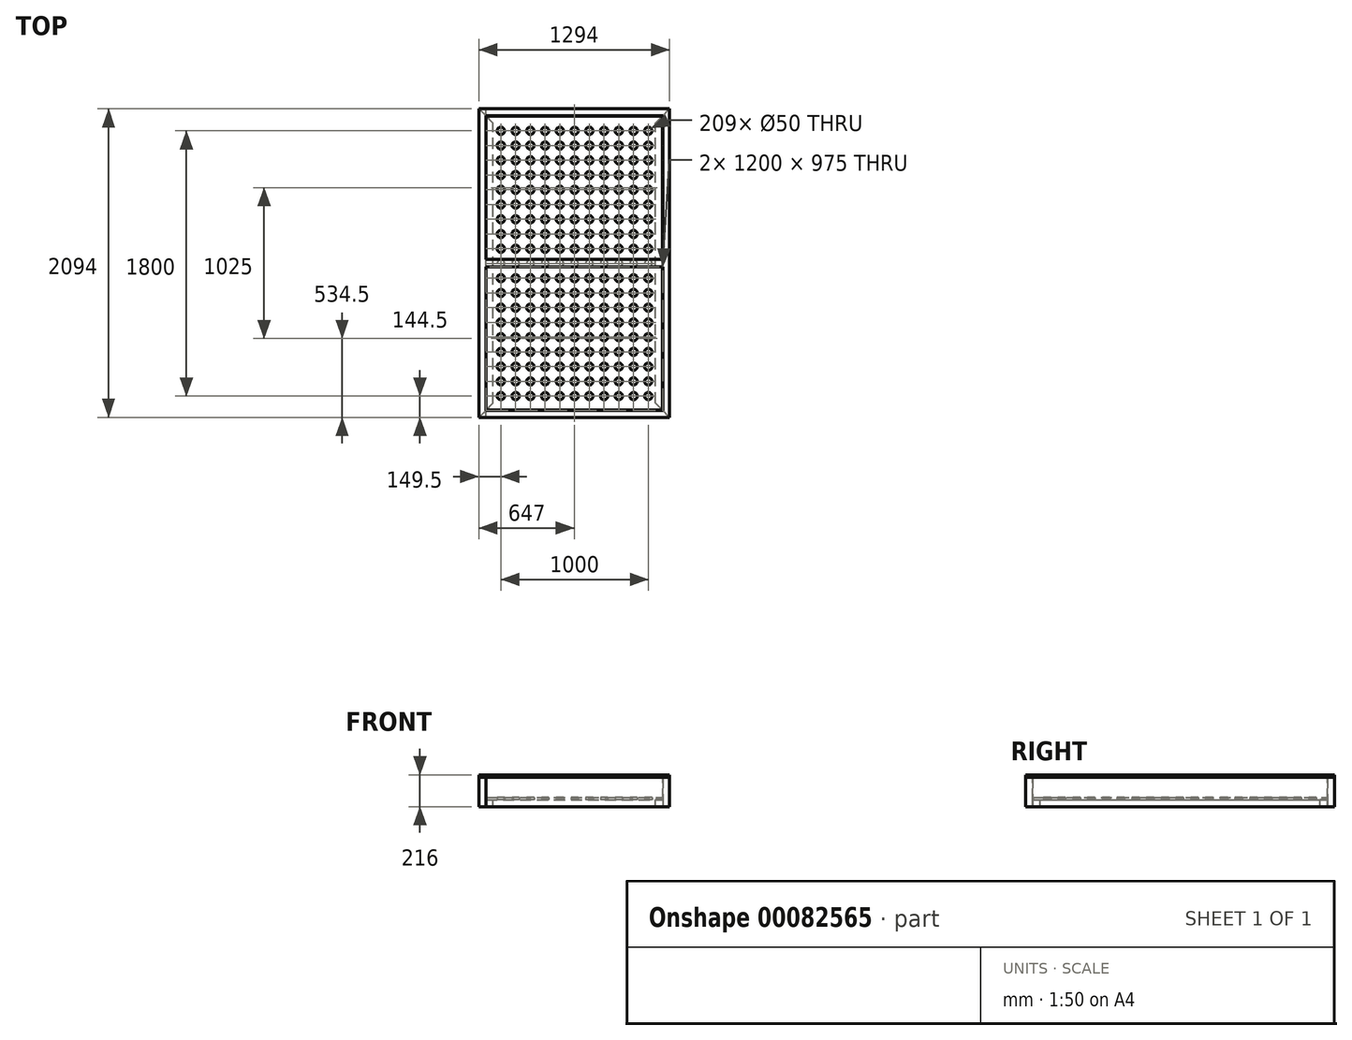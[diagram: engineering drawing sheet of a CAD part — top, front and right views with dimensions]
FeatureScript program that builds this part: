
annotation { "Feature Type Name" : "Feature", "Feature Type Description" : "" }
export const myFeature = defineFeature(function(context is Context, id is Id, definition is map)
    precondition{}
    {
        {
            var Q0;
            Q0=qCreatedBy(makeId("Front.planeOp"),FACE);
            var sketch = newSketch(context, id + "F0", { "sketchPlane" : qUnion([Q0])});
            skLineSegment(sketch, "E0.bottom", {"start": v(0, 0) * mm, "end": v(47, 0) * mm});
            skLineSegment(sketch, "E0.top", {"start": v(0, 200) * mm, "end": v(47, 200) * mm});
            skLineSegment(sketch, "E0.left", {"start": v(0, 0) * mm, "end": v(0, 200) * mm});
            skLineSegment(sketch, "E0.right", {"start": v(47, 0) * mm, "end": v(47, 200) * mm});
            skLineSegment(sketch, "E1", {"start": v(47, 0) * mm, "end": v(1247, 0) * mm, "construction": true});
            skLineSegment(sketch, "E2", {"start": v(647, 0) * mm, "end": v(647, 240.68) * mm, "construction": true});
            skLineSegment(sketch, "E3.bottom", {"start": v(47, 0) * mm, "end": v(97, 0) * mm});
            skLineSegment(sketch, "E3.top", {"start": v(47, 47) * mm, "end": v(97, 47) * mm});
            skLineSegment(sketch, "E3.left", {"start": v(47, 0) * mm, "end": v(47, 47) * mm});
            skLineSegment(sketch, "E3.right", {"start": v(97, 0) * mm, "end": v(97, 47) * mm});
            skLineSegment(sketch, "E4.MirrorCS", {"start": v(1294, 0) * mm, "end": v(1294, 200) * mm});
            skLineSegment(sketch, "E5.MirrorCS", {"start": v(1294, 0) * mm, "end": v(1247, 0) * mm});
            skLineSegment(sketch, "E6.MirrorCS", {"start": v(1247, 0) * mm, "end": v(1247, 200) * mm});
            skLineSegment(sketch, "E7.MirrorCS", {"start": v(1294, 200) * mm, "end": v(1247, 200) * mm});
            skLineSegment(sketch, "E8.MirrorCS", {"start": v(1247, 47) * mm, "end": v(1197, 47) * mm});
            skLineSegment(sketch, "E9.MirrorCS", {"start": v(1197, 0) * mm, "end": v(1197, 47) * mm});
            skLineSegment(sketch, "E10.MirrorCS", {"start": v(1247, 0) * mm, "end": v(1197, 0) * mm});
            skLineSegment(sketch, "E11.MirrorCS", {"start": v(1247, 0) * mm, "end": v(1247, 47) * mm});
            skSolve(sketch);
        }
        {
            var Q0;
            Q0 = qSketchRegion(id + "F0", true);
            extrude(context, id + "F1", {"entities" : qUnion([Q0]), "depth" : 2094 * mm});
        }
        {
            var Q0;
            Q0=makeQuery(id+"F1.opExtrude","SWEPT_FACE",FACE,{"disambiguationData":[OSD([sQuery(id+"F0.wireOp",EDGE,"E0.top")])]});
            var sketch = newSketch(context, id + "F2", { "sketchPlane" : qUnion([Q0])});
            skLineSegment(sketch, "E12", {"start": v(0, 0) * mm, "end": v(213.84, 0) * mm});
            skLineSegment(sketch, "E13", {"start": v(213.84, 0) * mm, "end": v(0, 0) * mm});
            skLineSegment(sketch, "E14", {"start": v(0, 0) * mm, "end": v(224.8, -224.8) * mm});
            skLineSegment(sketch, "E15", {"start": v(213.84, 0) * mm, "end": v(224.8, -224.8) * mm});
            skLineSegment(sketch, "E16", {"start": v(0, -2094) * mm, "end": v(120.3, -2094) * mm});
            skLineSegment(sketch, "E17", {"start": v(120.3, -2094) * mm, "end": v(0, -2094) * mm});
            skLineSegment(sketch, "E18", {"start": v(0, -2094) * mm, "end": v(152.65, -1941.35) * mm});
            skLineSegment(sketch, "E19", {"start": v(152.65, -1941.35) * mm, "end": v(120.3, -2094) * mm});
            skSolve(sketch);
        }
        {
            var Q0;
            {var subQ3=sQuery(id+"F2.wireOp",EDGE,"E15");Q0=makeQuery(id+"F2.imprint","IMPRINT",FACE,{"disambiguationData":[TD([[makeQuery(id+"F2.imprint","IMPRINT",EDGE,{"derivedFrom":subQ3}),-1.0]])]});}
            var Q1;
            {var subQ0=sQuery(id+"F2.wireOp",EDGE,"E14");var subQ1=sQuery(id+"F2.wireOp",EDGE,"E13");var subQ2=sQuery(id+"F0.wireOp",EDGE,"E0.top");var subQ3=makeQuery(id+"F2.imprint","INTERSECT",VERTEX,{"derivedFrom":[makeQuery(id+"F1.opExtrude","SWEPT_EDGE",EDGE,{"disambiguationData":[OSD([subQ2,sQuery(id+"F0.wireOp",EDGE,"E0.left")])]}),subQ1,subQ0]});Q1=makeQuery(id+"F2.imprint","IMPRINT",FACE,{"disambiguationData":[TD([[makeQuery(id+"F2.imprint","IMPRINT",EDGE,{"disambiguationData":[TD([[subQ3,-1.0]])],"derivedFrom":subQ1}),-1.0]])]});}
            var Q2;
            {var subQ0=sQuery(id+"F2.wireOp",EDGE,"E18");var subQ1=sQuery(id+"F2.wireOp",EDGE,"E17");var subQ2=sQuery(id+"F0.wireOp",EDGE,"E0.top");var subQ3=makeQuery(id+"F2.imprint","INTERSECT",VERTEX,{"derivedFrom":[makeQuery(id+"F1.opExtrude","SWEPT_EDGE",EDGE,{"disambiguationData":[OSD([subQ2,sQuery(id+"F0.wireOp",EDGE,"E0.left")])]}),subQ1,subQ0]});Q2=makeQuery(id+"F2.imprint","IMPRINT",FACE,{"disambiguationData":[TD([[makeQuery(id+"F2.imprint","IMPRINT",EDGE,{"disambiguationData":[TD([[subQ3,-1.0]])],"derivedFrom":subQ1}),1.0]])]});}
            var Q3;
            {var subQ3=sQuery(id+"F2.wireOp",EDGE,"E19");Q3=makeQuery(id+"F2.imprint","IMPRINT",FACE,{"disambiguationData":[TD([[makeQuery(id+"F2.imprint","IMPRINT",EDGE,{"derivedFrom":subQ3}),-1.0]])]});}
            extrude(context, id + "F3", {"entities" : qUnion([Q0, Q1, Q2, Q3]), "operationType" : NewBodyOperationType.REMOVE, "endBound" : BoundingType.THROUGH_ALL, "oppositeDirection" : true, "depth" : 25 * mm});
        }
        {
            var Q0;
            Q0=makeQuery(id+"F1.opExtrude","SWEPT_FACE",FACE,{"disambiguationData":[OSD([sQuery(id+"F0.wireOp",EDGE,"E7.MirrorCS")])]});
            var sketch = newSketch(context, id + "F4", { "sketchPlane" : qUnion([Q0])});
            skLineSegment(sketch, "E20", {"start": v(1294, 0) * mm, "end": v(937.7, 0) * mm});
            skLineSegment(sketch, "E21", {"start": v(937.7, 0) * mm, "end": v(937.7, -356.3) * mm});
            skLineSegment(sketch, "E22", {"start": v(937.7, -356.3) * mm, "end": v(1294, 0) * mm});
            skLineSegment(sketch, "E23", {"start": v(1294, -2094) * mm, "end": v(876.84, -2094) * mm});
            skLineSegment(sketch, "E24", {"start": v(876.84, -2094) * mm, "end": v(876.84, -1676.84) * mm});
            skLineSegment(sketch, "E25", {"start": v(876.84, -1676.84) * mm, "end": v(1294, -2094) * mm});
            skSolve(sketch);
        }
        {
            var Q0;
            Q0 = qSketchRegion(id + "F4", true);
            extrude(context, id + "F5", {"entities" : qUnion([Q0]), "operationType" : NewBodyOperationType.REMOVE, "endBound" : BoundingType.THROUGH_ALL, "oppositeDirection" : true, "depth" : 25 * mm});
        }
        {
            var Q0;
            Q0=qCreatedBy(makeId("Top.planeOp"),FACE);
            var sketch = newSketch(context, id + "F6", { "sketchPlane" : qUnion([Q0])});
            skLineSegment(sketch, "E26", {"start": v(0, 0) * mm, "end": v(1294, 0) * mm});
            skLineSegment(sketch, "E27", {"start": v(1294, 0) * mm, "end": v(1247, -47) * mm});
            skLineSegment(sketch, "E28", {"start": v(1247, -47) * mm, "end": v(47, -47) * mm});
            skLineSegment(sketch, "E29", {"start": v(47, -47) * mm, "end": v(0, 0) * mm});
            skLineSegment(sketch, "E30", {"start": v(1247, -2047) * mm, "end": v(1294, -2094) * mm});
            skLineSegment(sketch, "E31", {"start": v(1294, -2094) * mm, "end": v(0, -2094) * mm});
            skLineSegment(sketch, "E32", {"start": v(0, -2094) * mm, "end": v(47, -2047) * mm});
            skLineSegment(sketch, "E33", {"start": v(47, -2047) * mm, "end": v(1247, -2047) * mm});
            skLineSegment(sketch, "E34.0", {"start": v(0, 0) * mm, "end": v(47, -47) * mm});
            skSolve(sketch);
        }
        {
            var Q0;
            Q0 = qSketchRegion(id + "F6", true);
            extrude(context, id + "F7", {"entities" : qUnion([Q0]), "depth" : 200 * mm});
        }
        {
            var Q0;
            Q0=makeQuery(id+"F1.opExtrude","SWEPT_FACE",FACE,{"disambiguationData":[OSD([sQuery(id+"F0.wireOp",EDGE,"E8.MirrorCS")])]});
            var sketch = newSketch(context, id + "F8", { "sketchPlane" : qUnion([Q0])});
            skLineSegment(sketch, "E35.0", {"start": v(47, -2047) * mm, "end": v(47, -47) * mm});
            skLineSegment(sketch, "E36.0", {"start": v(1247, -2047) * mm, "end": v(1247, -47) * mm});
            skLineSegment(sketch, "E37", {"start": v(1247, -47) * mm, "end": v(47, -47) * mm});
            skLineSegment(sketch, "E38", {"start": v(47, -2047) * mm, "end": v(1247, -2047) * mm});
            skLineSegment(sketch, "E39.0", {"start": v(49.5, -2044.5) * mm, "end": v(49.5, -49.5) * mm});
            skLineSegment(sketch, "E39.1", {"start": v(49.5, -2044.5) * mm, "end": v(1244.5, -2044.5) * mm});
            skLineSegment(sketch, "E39.2", {"start": v(1244.5, -2044.5) * mm, "end": v(1244.5, -49.5) * mm});
            skLineSegment(sketch, "E39.3", {"start": v(1244.5, -49.5) * mm, "end": v(49.5, -49.5) * mm});
            skCircle(sketch, "E40", {"center": v(149.5, -149.5) * mm, "radius": 25 * mm});
            skCircle(sketch, "E41.0.1.0", {"center": v(149.5, -249.5) * mm, "radius": 25 * mm});
            skCircle(sketch, "E41.0.2.0", {"center": v(149.5, -349.5) * mm, "radius": 25 * mm});
            skCircle(sketch, "E41.0.3.0", {"center": v(149.5, -449.5) * mm, "radius": 25 * mm});
            skCircle(sketch, "E41.0.4.0", {"center": v(149.5, -549.5) * mm, "radius": 25 * mm});
            skCircle(sketch, "E41.0.5.0", {"center": v(149.5, -649.5) * mm, "radius": 25 * mm});
            skCircle(sketch, "E41.0.6.0", {"center": v(149.5, -749.5) * mm, "radius": 25 * mm});
            skCircle(sketch, "E41.0.7.0", {"center": v(149.5, -849.5) * mm, "radius": 25 * mm});
            skCircle(sketch, "E41.0.8.0", {"center": v(149.5, -949.5) * mm, "radius": 25 * mm});
            skCircle(sketch, "E41.0.9.0", {"center": v(149.5, -1049.5) * mm, "radius": 25 * mm});
            skCircle(sketch, "E41.0.10.0", {"center": v(149.5, -1149.5) * mm, "radius": 25 * mm});
            skCircle(sketch, "E41.0.11.0", {"center": v(149.5, -1249.5) * mm, "radius": 25 * mm});
            skCircle(sketch, "E41.0.12.0", {"center": v(149.5, -1349.5) * mm, "radius": 25 * mm});
            skCircle(sketch, "E41.0.13.0", {"center": v(149.5, -1449.5) * mm, "radius": 25 * mm});
            skCircle(sketch, "E41.0.14.0", {"center": v(149.5, -1549.5) * mm, "radius": 25 * mm});
            skCircle(sketch, "E41.0.15.0", {"center": v(149.5, -1649.5) * mm, "radius": 25 * mm});
            skCircle(sketch, "E41.0.16.0", {"center": v(149.5, -1749.5) * mm, "radius": 25 * mm});
            skCircle(sketch, "E41.0.17.0", {"center": v(149.5, -1849.5) * mm, "radius": 25 * mm});
            skCircle(sketch, "E41.0.18.0", {"center": v(149.5, -1949.5) * mm, "radius": 25 * mm});
            skCircle(sketch, "E41.1.0.0", {"center": v(249.5, -149.5) * mm, "radius": 25 * mm});
            skCircle(sketch, "E41.1.1.0", {"center": v(249.5, -249.5) * mm, "radius": 25 * mm});
            skCircle(sketch, "E41.1.2.0", {"center": v(249.5, -349.5) * mm, "radius": 25 * mm});
            skCircle(sketch, "E41.1.3.0", {"center": v(249.5, -449.5) * mm, "radius": 25 * mm});
            skCircle(sketch, "E41.1.4.0", {"center": v(249.5, -549.5) * mm, "radius": 25 * mm});
            skCircle(sketch, "E41.1.5.0", {"center": v(249.5, -649.5) * mm, "radius": 25 * mm});
            skCircle(sketch, "E41.1.6.0", {"center": v(249.5, -749.5) * mm, "radius": 25 * mm});
            skCircle(sketch, "E41.1.7.0", {"center": v(249.5, -849.5) * mm, "radius": 25 * mm});
            skCircle(sketch, "E41.1.8.0", {"center": v(249.5, -949.5) * mm, "radius": 25 * mm});
            skCircle(sketch, "E41.1.9.0", {"center": v(249.5, -1049.5) * mm, "radius": 25 * mm});
            skCircle(sketch, "E41.1.10.0", {"center": v(249.5, -1149.5) * mm, "radius": 25 * mm});
            skCircle(sketch, "E41.1.11.0", {"center": v(249.5, -1249.5) * mm, "radius": 25 * mm});
            skCircle(sketch, "E41.1.12.0", {"center": v(249.5, -1349.5) * mm, "radius": 25 * mm});
            skCircle(sketch, "E41.1.13.0", {"center": v(249.5, -1449.5) * mm, "radius": 25 * mm});
            skCircle(sketch, "E41.1.14.0", {"center": v(249.5, -1549.5) * mm, "radius": 25 * mm});
            skCircle(sketch, "E41.1.15.0", {"center": v(249.5, -1649.5) * mm, "radius": 25 * mm});
            skCircle(sketch, "E41.1.16.0", {"center": v(249.5, -1749.5) * mm, "radius": 25 * mm});
            skCircle(sketch, "E41.1.17.0", {"center": v(249.5, -1849.5) * mm, "radius": 25 * mm});
            skCircle(sketch, "E41.1.18.0", {"center": v(249.5, -1949.5) * mm, "radius": 25 * mm});
            skCircle(sketch, "E41.2.0.0", {"center": v(349.5, -149.5) * mm, "radius": 25 * mm});
            skCircle(sketch, "E41.2.1.0", {"center": v(349.5, -249.5) * mm, "radius": 25 * mm});
            skCircle(sketch, "E41.2.2.0", {"center": v(349.5, -349.5) * mm, "radius": 25 * mm});
            skCircle(sketch, "E41.2.3.0", {"center": v(349.5, -449.5) * mm, "radius": 25 * mm});
            skCircle(sketch, "E41.2.4.0", {"center": v(349.5, -549.5) * mm, "radius": 25 * mm});
            skCircle(sketch, "E41.2.5.0", {"center": v(349.5, -649.5) * mm, "radius": 25 * mm});
            skCircle(sketch, "E41.2.6.0", {"center": v(349.5, -749.5) * mm, "radius": 25 * mm});
            skCircle(sketch, "E41.2.7.0", {"center": v(349.5, -849.5) * mm, "radius": 25 * mm});
            skCircle(sketch, "E41.2.8.0", {"center": v(349.5, -949.5) * mm, "radius": 25 * mm});
            skCircle(sketch, "E41.2.9.0", {"center": v(349.5, -1049.5) * mm, "radius": 25 * mm});
            skCircle(sketch, "E41.2.10.0", {"center": v(349.5, -1149.5) * mm, "radius": 25 * mm});
            skCircle(sketch, "E41.2.11.0", {"center": v(349.5, -1249.5) * mm, "radius": 25 * mm});
            skCircle(sketch, "E41.2.12.0", {"center": v(349.5, -1349.5) * mm, "radius": 25 * mm});
            skCircle(sketch, "E41.2.13.0", {"center": v(349.5, -1449.5) * mm, "radius": 25 * mm});
            skCircle(sketch, "E41.2.14.0", {"center": v(349.5, -1549.5) * mm, "radius": 25 * mm});
            skCircle(sketch, "E41.2.15.0", {"center": v(349.5, -1649.5) * mm, "radius": 25 * mm});
            skCircle(sketch, "E41.2.16.0", {"center": v(349.5, -1749.5) * mm, "radius": 25 * mm});
            skCircle(sketch, "E41.2.17.0", {"center": v(349.5, -1849.5) * mm, "radius": 25 * mm});
            skCircle(sketch, "E41.2.18.0", {"center": v(349.5, -1949.5) * mm, "radius": 25 * mm});
            skCircle(sketch, "E41.3.0.0", {"center": v(449.5, -149.5) * mm, "radius": 25 * mm});
            skCircle(sketch, "E41.3.1.0", {"center": v(449.5, -249.5) * mm, "radius": 25 * mm});
            skCircle(sketch, "E41.3.2.0", {"center": v(449.5, -349.5) * mm, "radius": 25 * mm});
            skCircle(sketch, "E41.3.3.0", {"center": v(449.5, -449.5) * mm, "radius": 25 * mm});
            skCircle(sketch, "E41.3.4.0", {"center": v(449.5, -549.5) * mm, "radius": 25 * mm});
            skCircle(sketch, "E41.3.5.0", {"center": v(449.5, -649.5) * mm, "radius": 25 * mm});
            skCircle(sketch, "E41.3.6.0", {"center": v(449.5, -749.5) * mm, "radius": 25 * mm});
            skCircle(sketch, "E41.3.7.0", {"center": v(449.5, -849.5) * mm, "radius": 25 * mm});
            skCircle(sketch, "E41.3.8.0", {"center": v(449.5, -949.5) * mm, "radius": 25 * mm});
            skCircle(sketch, "E41.3.9.0", {"center": v(449.5, -1049.5) * mm, "radius": 25 * mm});
            skCircle(sketch, "E41.3.10.0", {"center": v(449.5, -1149.5) * mm, "radius": 25 * mm});
            skCircle(sketch, "E41.3.11.0", {"center": v(449.5, -1249.5) * mm, "radius": 25 * mm});
            skCircle(sketch, "E41.3.12.0", {"center": v(449.5, -1349.5) * mm, "radius": 25 * mm});
            skCircle(sketch, "E41.3.13.0", {"center": v(449.5, -1449.5) * mm, "radius": 25 * mm});
            skCircle(sketch, "E41.3.14.0", {"center": v(449.5, -1549.5) * mm, "radius": 25 * mm});
            skCircle(sketch, "E41.3.15.0", {"center": v(449.5, -1649.5) * mm, "radius": 25 * mm});
            skCircle(sketch, "E41.3.16.0", {"center": v(449.5, -1749.5) * mm, "radius": 25 * mm});
            skCircle(sketch, "E41.3.17.0", {"center": v(449.5, -1849.5) * mm, "radius": 25 * mm});
            skCircle(sketch, "E41.3.18.0", {"center": v(449.5, -1949.5) * mm, "radius": 25 * mm});
            skCircle(sketch, "E41.4.0.0", {"center": v(549.5, -149.5) * mm, "radius": 25 * mm});
            skCircle(sketch, "E41.4.1.0", {"center": v(549.5, -249.5) * mm, "radius": 25 * mm});
            skCircle(sketch, "E41.4.2.0", {"center": v(549.5, -349.5) * mm, "radius": 25 * mm});
            skCircle(sketch, "E41.4.3.0", {"center": v(549.5, -449.5) * mm, "radius": 25 * mm});
            skCircle(sketch, "E41.4.4.0", {"center": v(549.5, -549.5) * mm, "radius": 25 * mm});
            skCircle(sketch, "E41.4.5.0", {"center": v(549.5, -649.5) * mm, "radius": 25 * mm});
            skCircle(sketch, "E41.4.6.0", {"center": v(549.5, -749.5) * mm, "radius": 25 * mm});
            skCircle(sketch, "E41.4.7.0", {"center": v(549.5, -849.5) * mm, "radius": 25 * mm});
            skCircle(sketch, "E41.4.8.0", {"center": v(549.5, -949.5) * mm, "radius": 25 * mm});
            skCircle(sketch, "E41.4.9.0", {"center": v(549.5, -1049.5) * mm, "radius": 25 * mm});
            skCircle(sketch, "E41.4.10.0", {"center": v(549.5, -1149.5) * mm, "radius": 25 * mm});
            skCircle(sketch, "E41.4.11.0", {"center": v(549.5, -1249.5) * mm, "radius": 25 * mm});
            skCircle(sketch, "E41.4.12.0", {"center": v(549.5, -1349.5) * mm, "radius": 25 * mm});
            skCircle(sketch, "E41.4.13.0", {"center": v(549.5, -1449.5) * mm, "radius": 25 * mm});
            skCircle(sketch, "E41.4.14.0", {"center": v(549.5, -1549.5) * mm, "radius": 25 * mm});
            skCircle(sketch, "E41.4.15.0", {"center": v(549.5, -1649.5) * mm, "radius": 25 * mm});
            skCircle(sketch, "E41.4.16.0", {"center": v(549.5, -1749.5) * mm, "radius": 25 * mm});
            skCircle(sketch, "E41.4.17.0", {"center": v(549.5, -1849.5) * mm, "radius": 25 * mm});
            skCircle(sketch, "E41.4.18.0", {"center": v(549.5, -1949.5) * mm, "radius": 25 * mm});
            skCircle(sketch, "E41.5.0.0", {"center": v(649.5, -149.5) * mm, "radius": 25 * mm});
            skCircle(sketch, "E41.5.1.0", {"center": v(649.5, -249.5) * mm, "radius": 25 * mm});
            skCircle(sketch, "E41.5.2.0", {"center": v(649.5, -349.5) * mm, "radius": 25 * mm});
            skCircle(sketch, "E41.5.3.0", {"center": v(649.5, -449.5) * mm, "radius": 25 * mm});
            skCircle(sketch, "E41.5.4.0", {"center": v(649.5, -549.5) * mm, "radius": 25 * mm});
            skCircle(sketch, "E41.5.5.0", {"center": v(649.5, -649.5) * mm, "radius": 25 * mm});
            skCircle(sketch, "E41.5.6.0", {"center": v(649.5, -749.5) * mm, "radius": 25 * mm});
            skCircle(sketch, "E41.5.7.0", {"center": v(649.5, -849.5) * mm, "radius": 25 * mm});
            skCircle(sketch, "E41.5.8.0", {"center": v(649.5, -949.5) * mm, "radius": 25 * mm});
            skCircle(sketch, "E41.5.9.0", {"center": v(649.5, -1049.5) * mm, "radius": 25 * mm});
            skCircle(sketch, "E41.5.10.0", {"center": v(649.5, -1149.5) * mm, "radius": 25 * mm});
            skCircle(sketch, "E41.5.11.0", {"center": v(649.5, -1249.5) * mm, "radius": 25 * mm});
            skCircle(sketch, "E41.5.12.0", {"center": v(649.5, -1349.5) * mm, "radius": 25 * mm});
            skCircle(sketch, "E41.5.13.0", {"center": v(649.5, -1449.5) * mm, "radius": 25 * mm});
            skCircle(sketch, "E41.5.14.0", {"center": v(649.5, -1549.5) * mm, "radius": 25 * mm});
            skCircle(sketch, "E41.5.15.0", {"center": v(649.5, -1649.5) * mm, "radius": 25 * mm});
            skCircle(sketch, "E41.5.16.0", {"center": v(649.5, -1749.5) * mm, "radius": 25 * mm});
            skCircle(sketch, "E41.5.17.0", {"center": v(649.5, -1849.5) * mm, "radius": 25 * mm});
            skCircle(sketch, "E41.5.18.0", {"center": v(649.5, -1949.5) * mm, "radius": 25 * mm});
            skCircle(sketch, "E41.6.0.0", {"center": v(749.5, -149.5) * mm, "radius": 25 * mm});
            skCircle(sketch, "E41.6.1.0", {"center": v(749.5, -249.5) * mm, "radius": 25 * mm});
            skCircle(sketch, "E41.6.2.0", {"center": v(749.5, -349.5) * mm, "radius": 25 * mm});
            skCircle(sketch, "E41.6.3.0", {"center": v(749.5, -449.5) * mm, "radius": 25 * mm});
            skCircle(sketch, "E41.6.4.0", {"center": v(749.5, -549.5) * mm, "radius": 25 * mm});
            skCircle(sketch, "E41.6.5.0", {"center": v(749.5, -649.5) * mm, "radius": 25 * mm});
            skCircle(sketch, "E41.6.6.0", {"center": v(749.5, -749.5) * mm, "radius": 25 * mm});
            skCircle(sketch, "E41.6.7.0", {"center": v(749.5, -849.5) * mm, "radius": 25 * mm});
            skCircle(sketch, "E41.6.8.0", {"center": v(749.5, -949.5) * mm, "radius": 25 * mm});
            skCircle(sketch, "E41.6.9.0", {"center": v(749.5, -1049.5) * mm, "radius": 25 * mm});
            skCircle(sketch, "E41.6.10.0", {"center": v(749.5, -1149.5) * mm, "radius": 25 * mm});
            skCircle(sketch, "E41.6.11.0", {"center": v(749.5, -1249.5) * mm, "radius": 25 * mm});
            skCircle(sketch, "E41.6.12.0", {"center": v(749.5, -1349.5) * mm, "radius": 25 * mm});
            skCircle(sketch, "E41.6.13.0", {"center": v(749.5, -1449.5) * mm, "radius": 25 * mm});
            skCircle(sketch, "E41.6.14.0", {"center": v(749.5, -1549.5) * mm, "radius": 25 * mm});
            skCircle(sketch, "E41.6.15.0", {"center": v(749.5, -1649.5) * mm, "radius": 25 * mm});
            skCircle(sketch, "E41.6.16.0", {"center": v(749.5, -1749.5) * mm, "radius": 25 * mm});
            skCircle(sketch, "E41.6.17.0", {"center": v(749.5, -1849.5) * mm, "radius": 25 * mm});
            skCircle(sketch, "E41.6.18.0", {"center": v(749.5, -1949.5) * mm, "radius": 25 * mm});
            skCircle(sketch, "E41.7.0.0", {"center": v(849.5, -149.5) * mm, "radius": 25 * mm});
            skCircle(sketch, "E41.7.1.0", {"center": v(849.5, -249.5) * mm, "radius": 25 * mm});
            skCircle(sketch, "E41.7.2.0", {"center": v(849.5, -349.5) * mm, "radius": 25 * mm});
            skCircle(sketch, "E41.7.3.0", {"center": v(849.5, -449.5) * mm, "radius": 25 * mm});
            skCircle(sketch, "E41.7.4.0", {"center": v(849.5, -549.5) * mm, "radius": 25 * mm});
            skCircle(sketch, "E41.7.5.0", {"center": v(849.5, -649.5) * mm, "radius": 25 * mm});
            skCircle(sketch, "E41.7.6.0", {"center": v(849.5, -749.5) * mm, "radius": 25 * mm});
            skCircle(sketch, "E41.7.7.0", {"center": v(849.5, -849.5) * mm, "radius": 25 * mm});
            skCircle(sketch, "E41.7.8.0", {"center": v(849.5, -949.5) * mm, "radius": 25 * mm});
            skCircle(sketch, "E41.7.9.0", {"center": v(849.5, -1049.5) * mm, "radius": 25 * mm});
            skCircle(sketch, "E41.7.10.0", {"center": v(849.5, -1149.5) * mm, "radius": 25 * mm});
            skCircle(sketch, "E41.7.11.0", {"center": v(849.5, -1249.5) * mm, "radius": 25 * mm});
            skCircle(sketch, "E41.7.12.0", {"center": v(849.5, -1349.5) * mm, "radius": 25 * mm});
            skCircle(sketch, "E41.7.13.0", {"center": v(849.5, -1449.5) * mm, "radius": 25 * mm});
            skCircle(sketch, "E41.7.14.0", {"center": v(849.5, -1549.5) * mm, "radius": 25 * mm});
            skCircle(sketch, "E41.7.15.0", {"center": v(849.5, -1649.5) * mm, "radius": 25 * mm});
            skCircle(sketch, "E41.7.16.0", {"center": v(849.5, -1749.5) * mm, "radius": 25 * mm});
            skCircle(sketch, "E41.7.17.0", {"center": v(849.5, -1849.5) * mm, "radius": 25 * mm});
            skCircle(sketch, "E41.7.18.0", {"center": v(849.5, -1949.5) * mm, "radius": 25 * mm});
            skCircle(sketch, "E41.8.0.0", {"center": v(949.5, -149.5) * mm, "radius": 25 * mm});
            skCircle(sketch, "E41.8.1.0", {"center": v(949.5, -249.5) * mm, "radius": 25 * mm});
            skCircle(sketch, "E41.8.2.0", {"center": v(949.5, -349.5) * mm, "radius": 25 * mm});
            skCircle(sketch, "E41.8.3.0", {"center": v(949.5, -449.5) * mm, "radius": 25 * mm});
            skCircle(sketch, "E41.8.4.0", {"center": v(949.5, -549.5) * mm, "radius": 25 * mm});
            skCircle(sketch, "E41.8.5.0", {"center": v(949.5, -649.5) * mm, "radius": 25 * mm});
            skCircle(sketch, "E41.8.6.0", {"center": v(949.5, -749.5) * mm, "radius": 25 * mm});
            skCircle(sketch, "E41.8.7.0", {"center": v(949.5, -849.5) * mm, "radius": 25 * mm});
            skCircle(sketch, "E41.8.8.0", {"center": v(949.5, -949.5) * mm, "radius": 25 * mm});
            skCircle(sketch, "E41.8.9.0", {"center": v(949.5, -1049.5) * mm, "radius": 25 * mm});
            skCircle(sketch, "E41.8.10.0", {"center": v(949.5, -1149.5) * mm, "radius": 25 * mm});
            skCircle(sketch, "E41.8.11.0", {"center": v(949.5, -1249.5) * mm, "radius": 25 * mm});
            skCircle(sketch, "E41.8.12.0", {"center": v(949.5, -1349.5) * mm, "radius": 25 * mm});
            skCircle(sketch, "E41.8.13.0", {"center": v(949.5, -1449.5) * mm, "radius": 25 * mm});
            skCircle(sketch, "E41.8.14.0", {"center": v(949.5, -1549.5) * mm, "radius": 25 * mm});
            skCircle(sketch, "E41.8.15.0", {"center": v(949.5, -1649.5) * mm, "radius": 25 * mm});
            skCircle(sketch, "E41.8.16.0", {"center": v(949.5, -1749.5) * mm, "radius": 25 * mm});
            skCircle(sketch, "E41.8.17.0", {"center": v(949.5, -1849.5) * mm, "radius": 25 * mm});
            skCircle(sketch, "E41.8.18.0", {"center": v(949.5, -1949.5) * mm, "radius": 25 * mm});
            skCircle(sketch, "E41.9.0.0", {"center": v(1049.5, -149.5) * mm, "radius": 25 * mm});
            skCircle(sketch, "E41.9.1.0", {"center": v(1049.5, -249.5) * mm, "radius": 25 * mm});
            skCircle(sketch, "E41.9.2.0", {"center": v(1049.5, -349.5) * mm, "radius": 25 * mm});
            skCircle(sketch, "E41.9.3.0", {"center": v(1049.5, -449.5) * mm, "radius": 25 * mm});
            skCircle(sketch, "E41.9.4.0", {"center": v(1049.5, -549.5) * mm, "radius": 25 * mm});
            skCircle(sketch, "E41.9.5.0", {"center": v(1049.5, -649.5) * mm, "radius": 25 * mm});
            skCircle(sketch, "E41.9.6.0", {"center": v(1049.5, -749.5) * mm, "radius": 25 * mm});
            skCircle(sketch, "E41.9.7.0", {"center": v(1049.5, -849.5) * mm, "radius": 25 * mm});
            skCircle(sketch, "E41.9.8.0", {"center": v(1049.5, -949.5) * mm, "radius": 25 * mm});
            skCircle(sketch, "E41.9.9.0", {"center": v(1049.5, -1049.5) * mm, "radius": 25 * mm});
            skCircle(sketch, "E41.9.10.0", {"center": v(1049.5, -1149.5) * mm, "radius": 25 * mm});
            skCircle(sketch, "E41.9.11.0", {"center": v(1049.5, -1249.5) * mm, "radius": 25 * mm});
            skCircle(sketch, "E41.9.12.0", {"center": v(1049.5, -1349.5) * mm, "radius": 25 * mm});
            skCircle(sketch, "E41.9.13.0", {"center": v(1049.5, -1449.5) * mm, "radius": 25 * mm});
            skCircle(sketch, "E41.9.14.0", {"center": v(1049.5, -1549.5) * mm, "radius": 25 * mm});
            skCircle(sketch, "E41.9.15.0", {"center": v(1049.5, -1649.5) * mm, "radius": 25 * mm});
            skCircle(sketch, "E41.9.16.0", {"center": v(1049.5, -1749.5) * mm, "radius": 25 * mm});
            skCircle(sketch, "E41.9.17.0", {"center": v(1049.5, -1849.5) * mm, "radius": 25 * mm});
            skCircle(sketch, "E41.9.18.0", {"center": v(1049.5, -1949.5) * mm, "radius": 25 * mm});
            skCircle(sketch, "E41.10.0.0", {"center": v(1149.5, -149.5) * mm, "radius": 25 * mm});
            skCircle(sketch, "E41.10.1.0", {"center": v(1149.5, -249.5) * mm, "radius": 25 * mm});
            skCircle(sketch, "E41.10.2.0", {"center": v(1149.5, -349.5) * mm, "radius": 25 * mm});
            skCircle(sketch, "E41.10.3.0", {"center": v(1149.5, -449.5) * mm, "radius": 25 * mm});
            skCircle(sketch, "E41.10.4.0", {"center": v(1149.5, -549.5) * mm, "radius": 25 * mm});
            skCircle(sketch, "E41.10.5.0", {"center": v(1149.5, -649.5) * mm, "radius": 25 * mm});
            skCircle(sketch, "E41.10.6.0", {"center": v(1149.5, -749.5) * mm, "radius": 25 * mm});
            skCircle(sketch, "E41.10.7.0", {"center": v(1149.5, -849.5) * mm, "radius": 25 * mm});
            skCircle(sketch, "E41.10.8.0", {"center": v(1149.5, -949.5) * mm, "radius": 25 * mm});
            skCircle(sketch, "E41.10.9.0", {"center": v(1149.5, -1049.5) * mm, "radius": 25 * mm});
            skCircle(sketch, "E41.10.10.0", {"center": v(1149.5, -1149.5) * mm, "radius": 25 * mm});
            skCircle(sketch, "E41.10.11.0", {"center": v(1149.5, -1249.5) * mm, "radius": 25 * mm});
            skCircle(sketch, "E41.10.12.0", {"center": v(1149.5, -1349.5) * mm, "radius": 25 * mm});
            skCircle(sketch, "E41.10.13.0", {"center": v(1149.5, -1449.5) * mm, "radius": 25 * mm});
            skCircle(sketch, "E41.10.14.0", {"center": v(1149.5, -1549.5) * mm, "radius": 25 * mm});
            skCircle(sketch, "E41.10.15.0", {"center": v(1149.5, -1649.5) * mm, "radius": 25 * mm});
            skCircle(sketch, "E41.10.16.0", {"center": v(1149.5, -1749.5) * mm, "radius": 25 * mm});
            skCircle(sketch, "E41.10.17.0", {"center": v(1149.5, -1849.5) * mm, "radius": 25 * mm});
            skCircle(sketch, "E41.10.18.0", {"center": v(1149.5, -1949.5) * mm, "radius": 25 * mm});
            skLineSegment(sketch, "E41.direction1", {"start": v(149.5, -149.5) * mm, "end": v(249.5, -149.5) * mm, "construction": true});
            skLineSegment(sketch, "E41.direction2", {"start": v(149.5, -149.5) * mm, "end": v(149.5, -249.5) * mm, "construction": true});
            skSolve(sketch);
        }
        {
            var Q0;
            {var subQ4=sQuery(id+"F8.wireOp",EDGE,"E39.1");Q0=makeQuery(id+"F8.imprint","IMPRINT",FACE,{"disambiguationData":[TD([[makeQuery(id+"F8.imprint","IMPRINT",EDGE,{"derivedFrom":subQ4}),1.0]])]});}
            var Q1;
            {var subQ0=sQuery(id+"F8.wireOp",EDGE,"E39.2");Q1=makeQuery(id+"F8.imprint","IMPRINT",FACE,{"disambiguationData":[TD([[makeQuery(id+"F8.imprint","IMPRINT",EDGE,{"derivedFrom":subQ0}),1.0]])]});}
            extrude(context, id + "F9", {"entities" : qUnion([Q0, Q1]), "depth" : 16 * mm});
        }
        {
            var Q0;
            Q0=makeQuery(id+"F1.opExtrude","SWEPT_FACE",FACE,{"disambiguationData":[OSD([sQuery(id+"F0.wireOp",EDGE,"E0.top")])]});
            var sketch = newSketch(context, id + "F10", { "sketchPlane" : qUnion([Q0])});
            skLineSegment(sketch, "E42.0.0", {"start": v(0, 0) * mm, "end": v(0, -2094) * mm});
            skLineSegment(sketch, "E42.0.2", {"start": v(47, -2047) * mm, "end": v(47, -47) * mm});
            skLineSegment(sketch, "E43.0.0", {"start": v(1294, 0) * mm, "end": v(0, 0) * mm});
            skLineSegment(sketch, "E43.0.2", {"start": v(47, -47) * mm, "end": v(1247, -47) * mm});
            skLineSegment(sketch, "E44.0.0", {"start": v(1247, -47) * mm, "end": v(1247, -2047) * mm});
            skLineSegment(sketch, "E44.0.2", {"start": v(1294, -2094) * mm, "end": v(1294, 0) * mm});
            skLineSegment(sketch, "E45.0.1", {"start": v(1247, -2047) * mm, "end": v(47, -2047) * mm});
            skLineSegment(sketch, "E45.0.3", {"start": v(0, -2094) * mm, "end": v(1294, -2094) * mm});
            skLineSegment(sketch, "E46", {"start": v(47, -47) * mm, "end": v(47, 0) * mm});
            skLineSegment(sketch, "E47", {"start": v(1247, -47) * mm, "end": v(1247, 0) * mm});
            skLineSegment(sketch, "E48", {"start": v(1247, -2047) * mm, "end": v(1247, -2094) * mm});
            skLineSegment(sketch, "E49", {"start": v(47, -2047) * mm, "end": v(47, -2094) * mm});
            skLineSegment(sketch, "E50.bottom", {"start": v(47, -1022) * mm, "end": v(1247, -1022) * mm});
            skLineSegment(sketch, "E50.top", {"start": v(47, -1072) * mm, "end": v(1247, -1072) * mm});
            skLineSegment(sketch, "E50.left", {"start": v(47, -1022) * mm, "end": v(47, -1072) * mm});
            skLineSegment(sketch, "E50.right", {"start": v(1247, -1022) * mm, "end": v(1247, -1072) * mm});
            skSolve(sketch);
        }
        {
            var Q0;
            Q0 = qSketchRegion(id + "F10", true);
            var Q1;
            Q1=makeQuery(id+"F10.imprint","IMPRINT",FACE,{"disambiguationData":[TD([[makeQuery(id+"F10.imprint","IMPRINT",EDGE,{"derivedFrom":sQuery(id+"F10.wireOp",EDGE,"E50.bottom")}),-1.0]])]});
            extrude(context, id + "F11", {"entities" : qUnion([Q0, Q1]), "depth" : 16 * mm});
        }
    });
